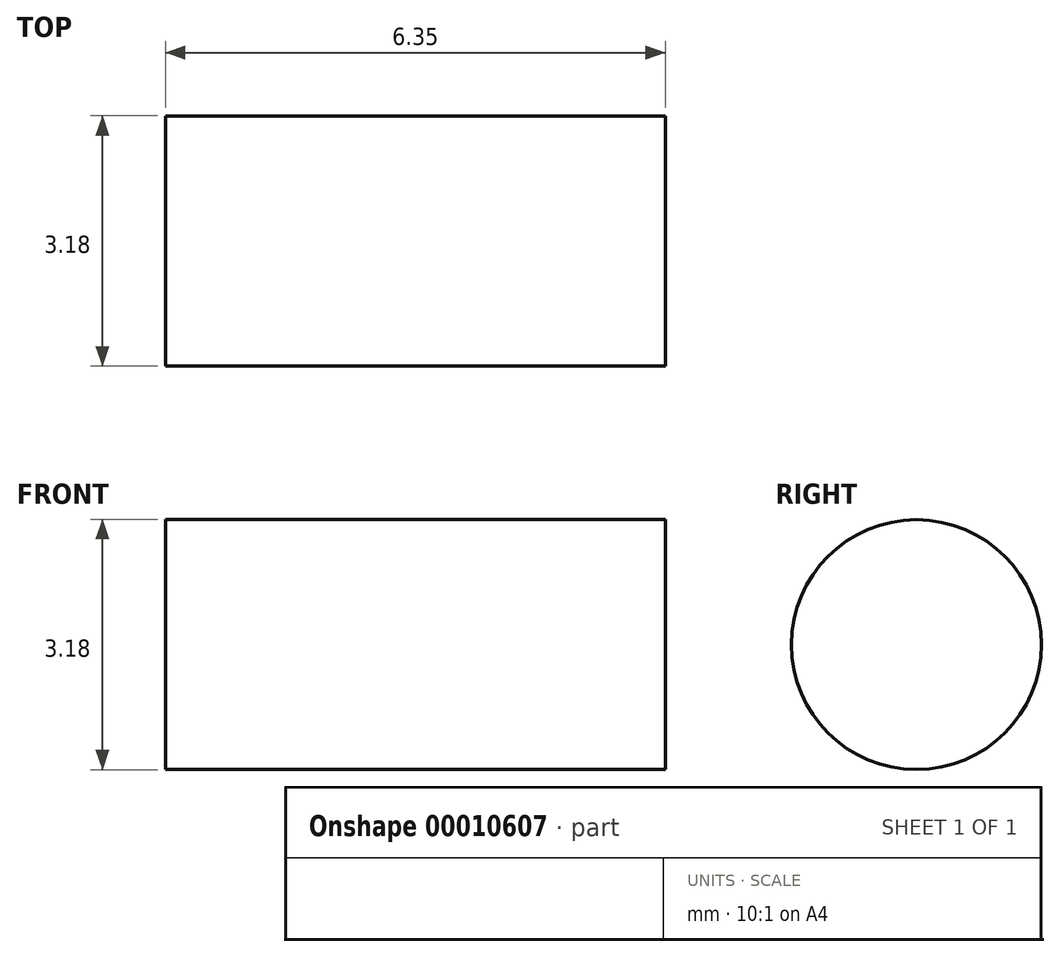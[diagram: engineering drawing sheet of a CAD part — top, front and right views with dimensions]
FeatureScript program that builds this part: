
annotation { "Feature Type Name" : "Feature", "Feature Type Description" : "" }
export const myFeature = defineFeature(function(context is Context, id is Id, definition is map)
    precondition{}
    {
        {
            var Q0;
            Q0=qCreatedBy(makeId("Right.planeOp"),FACE);
            var sketch = newSketch(context, id + "F0", { "sketchPlane" : qUnion([Q0])});
            skCircle(sketch, "E0", {"center": v(0, 0) * mm, "radius": 1.59 * mm});
            skSolve(sketch);
        }
        {
            var Q0;
            Q0=qSketchRegion(id+"F0",true);
            extrude(context, id + "F1", {"entities" : qUnion([Q0]), "depth" : 6.35 * mm});
        }
    });
